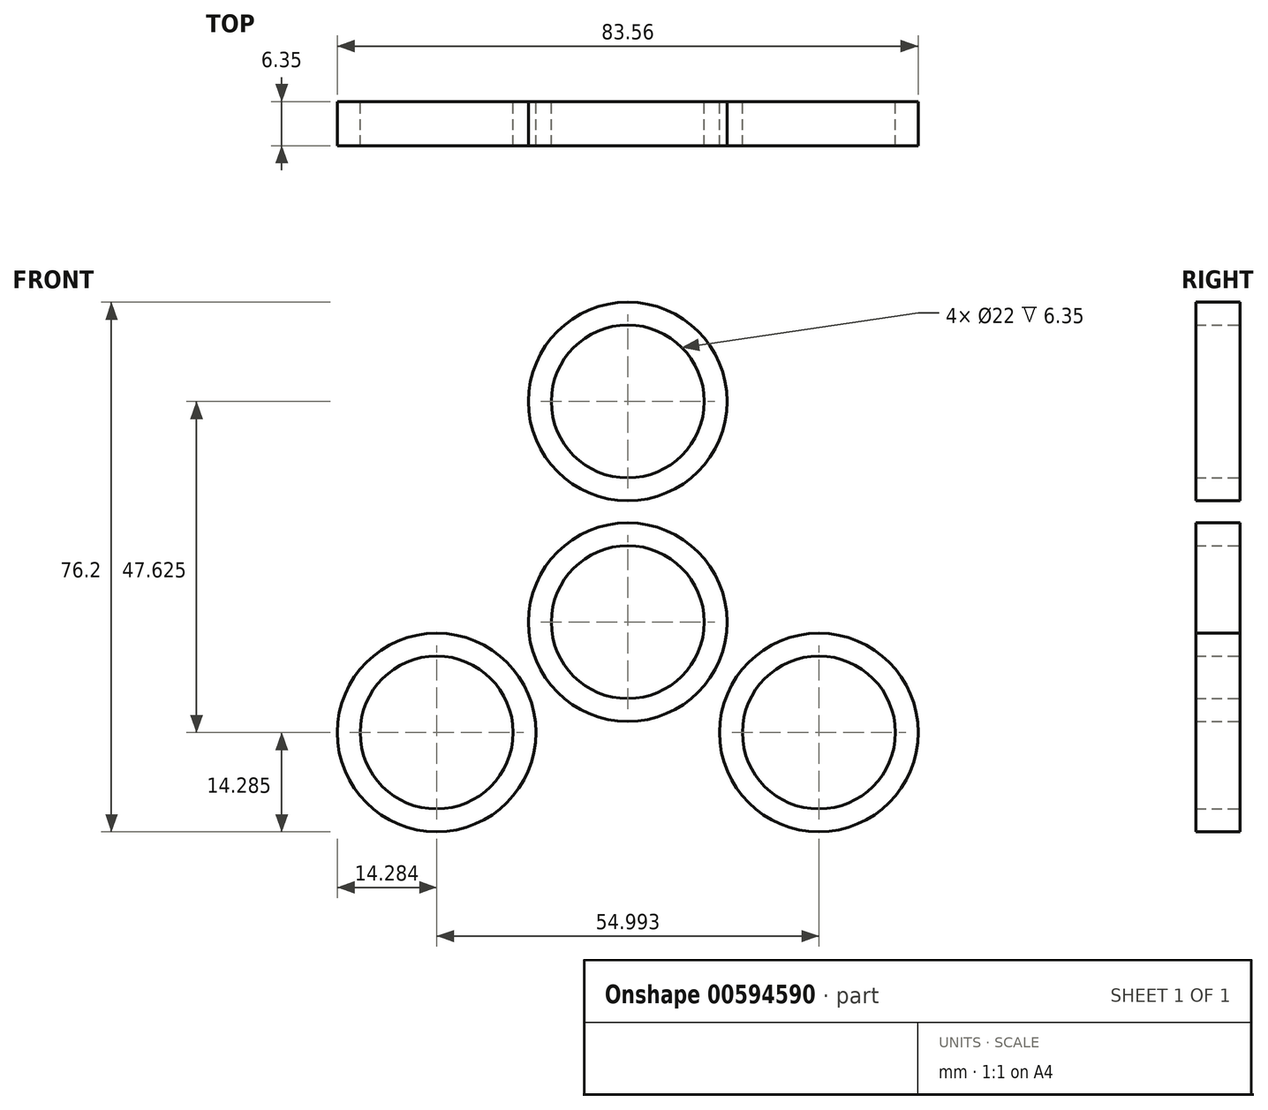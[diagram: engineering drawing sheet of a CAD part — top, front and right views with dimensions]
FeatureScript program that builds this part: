
annotation { "Feature Type Name" : "Feature", "Feature Type Description" : "" }
export const myFeature = defineFeature(function(context is Context, id is Id, definition is map)
    precondition{}
    {
        {
            var Q0;
            Q0=qCreatedBy(makeId("Front.planeOp"),FACE);
            var sketch = newSketch(context, id + "F0", { "sketchPlane" : qUnion([Q0])});
            skCircle(sketch, "E0", {"center": v(0, 0) * mm, "radius": 14.29 * mm});
            skCircle(sketch, "E1", {"center": v(0, 0) * mm, "radius": 11 * mm});
            skCircle(sketch, "E2", {"center": v(0, 31.75) * mm, "radius": 14.29 * mm});
            skCircle(sketch, "E3", {"center": v(0, 31.75) * mm, "radius": 11 * mm});
            skSolve(sketch);
        }
        {
            var Q0;
            Q0=qCreatedBy(makeId("Front.planeOp"),FACE);
            var sketch = newSketch(context, id + "F1", { "sketchPlane" : qUnion([Q0])});
            skPoint(sketch, "E4.center.orphan", {"position": v(-27.95, -15.95) * mm});
            skPoint(sketch, "E5.center.orphan", {"position": v(26.66, -17.15) * mm});
            skCircle(sketch, "E6.0", {"center": v(0, 31.75) * mm, "radius": 11 * mm});
            skCircle(sketch, "E7.0", {"center": v(0, 31.75) * mm, "radius": 14.29 * mm});
            skCircle(sketch, "E8.0", {"center": v(0, 0) * mm, "radius": 14.29 * mm});
            skCircle(sketch, "E9.0.0", {"center": v(0, 0) * mm, "radius": 11 * mm});
            skCircle(sketch, "E10.1.0", {"center": v(-27.5, -15.87) * mm, "radius": 14.29 * mm});
            skCircle(sketch, "E10.1.1", {"center": v(-27.5, -15.87) * mm, "radius": 11 * mm});
            skCircle(sketch, "E10.1.2", {"center": v(-27.5, -15.87) * mm, "radius": 14.29 * mm});
            skCircle(sketch, "E10.2.0", {"center": v(27.5, -15.88) * mm, "radius": 14.29 * mm});
            skCircle(sketch, "E10.2.1", {"center": v(27.5, -15.88) * mm, "radius": 11 * mm});
            skCircle(sketch, "E10.2.2", {"center": v(27.5, -15.88) * mm, "radius": 14.29 * mm});
            skSolve(sketch);
        }
        {
            var Q0;
            Q0=qCreatedBy(makeId("Front.planeOp"),FACE);
            var sketch = newSketch(context, id + "F2", { "sketchPlane" : qUnion([Q0])});
            skCircle(sketch, "E11.0", {"center": v(-27.5, -15.87) * mm, "radius": 11 * mm});
            skCircle(sketch, "E11.1", {"center": v(-27.5, -15.87) * mm, "radius": 14.29 * mm});
            skCircle(sketch, "E11.2", {"center": v(0, 0) * mm, "radius": 14.29 * mm});
            skCircle(sketch, "E11.3", {"center": v(0, 31.75) * mm, "radius": 14.29 * mm});
            skCircle(sketch, "E11.4", {"center": v(27.5, -15.88) * mm, "radius": 14.29 * mm});
            skCircle(sketch, "E11.5", {"center": v(27.5, -15.88) * mm, "radius": 11 * mm});
            skCircle(sketch, "E11.6", {"center": v(0, 0) * mm, "radius": 11 * mm});
            skCircle(sketch, "E11.7", {"center": v(0, 31.75) * mm, "radius": 11 * mm});
            skCircle(sketch, "E11.8", {"center": v(0, 31.75) * mm, "radius": 11 * mm});
            skCircle(sketch, "E11.9", {"center": v(0, 0) * mm, "radius": 11 * mm});
            skCircle(sketch, "E11.10", {"center": v(0, 0) * mm, "radius": 14.29 * mm});
            skCircle(sketch, "E11.11", {"center": v(27.5, -15.88) * mm, "radius": 14.29 * mm});
            skCircle(sketch, "E11.12", {"center": v(-27.5, -15.87) * mm, "radius": 14.29 * mm});
            skCircle(sketch, "E11.13", {"center": v(0, 31.75) * mm, "radius": 14.29 * mm});
            skCircle(sketch, "E11.14", {"center": v(0, 31.75) * mm, "radius": 14.29 * mm});
            skArc(sketch, "E12", {"start": v(13.87, 28.33) * mm, "mid": v(16.54, 9.55) * mm, "end": v(31.47, -2.15) * mm});
            skArc(sketch, "E13", {"start": v(17.6, -26.18) * mm, "mid": v(0, -19.1) * mm, "end": v(-17.6, -26.18) * mm});
            skArc(sketch, "E14", {"start": v(-31.47, -2.15) * mm, "mid": v(-16.54, 9.55) * mm, "end": v(-13.87, 28.33) * mm});
            skText(sketch, "E15", { "text": "G H", "fontName": "OpenSans-BoldItalic.ttf"});
            const initialGuessF2  = {"E15": [-0.01288, 0.01488, 1, 0, 0.00245]};
            skSetInitialGuess(sketch, initialGuessF2);
            skSolve(sketch);
        }
        {
            var Q0;
            Q0=makeQuery(id+"F0.imprint","IMPRINT",FACE,{"disambiguationData":[TD([[makeQuery(id+"F0.imprint","IMPRINT",EDGE,{"derivedFrom":sQuery(id+"F0.wireOp",EDGE,"E2")}),1.0]])]});
            var Q1;
            Q1=makeQuery(id+"F1.imprint","IMPRINT",FACE,{"disambiguationData":[TD([[makeQuery(id+"F1.imprint","IMPRINT",EDGE,{"derivedFrom":sQuery(id+"F1.wireOp",EDGE,"E10.1.1")}),-1.0]])]});
            var Q2;
            Q2=makeQuery(id+"F1.imprint","IMPRINT",FACE,{"disambiguationData":[TD([[makeQuery(id+"F1.imprint","IMPRINT",EDGE,{"derivedFrom":sQuery(id+"F1.wireOp",EDGE,"E10.2.1")}),-1.0]])]});
            var Q3;
            Q3=makeQuery(id+"F2.imprint","IMPRINT",FACE,{"disambiguationData":[TD([[makeQuery(id+"F2.imprint","IMPRINT",EDGE,{"derivedFrom":sQuery(id+"F2.wireOp",EDGE,"E11.10")}),-1.0]])]});
            var Q4;
            Q4=makeQuery(id+"F0.imprint","IMPRINT",FACE,{"disambiguationData":[TD([[makeQuery(id+"F0.imprint","IMPRINT",EDGE,{"derivedFrom":sQuery(id+"F0.wireOp",EDGE,"E0")}),1.0]])]});
            extrude(context, id + "F3", {"entities" : qUnion([Q0, Q1, Q2, Q3, Q4]), "depth" : 6.35 * mm, "offsetDistance" : 25.4 * mm});
        }
    });
